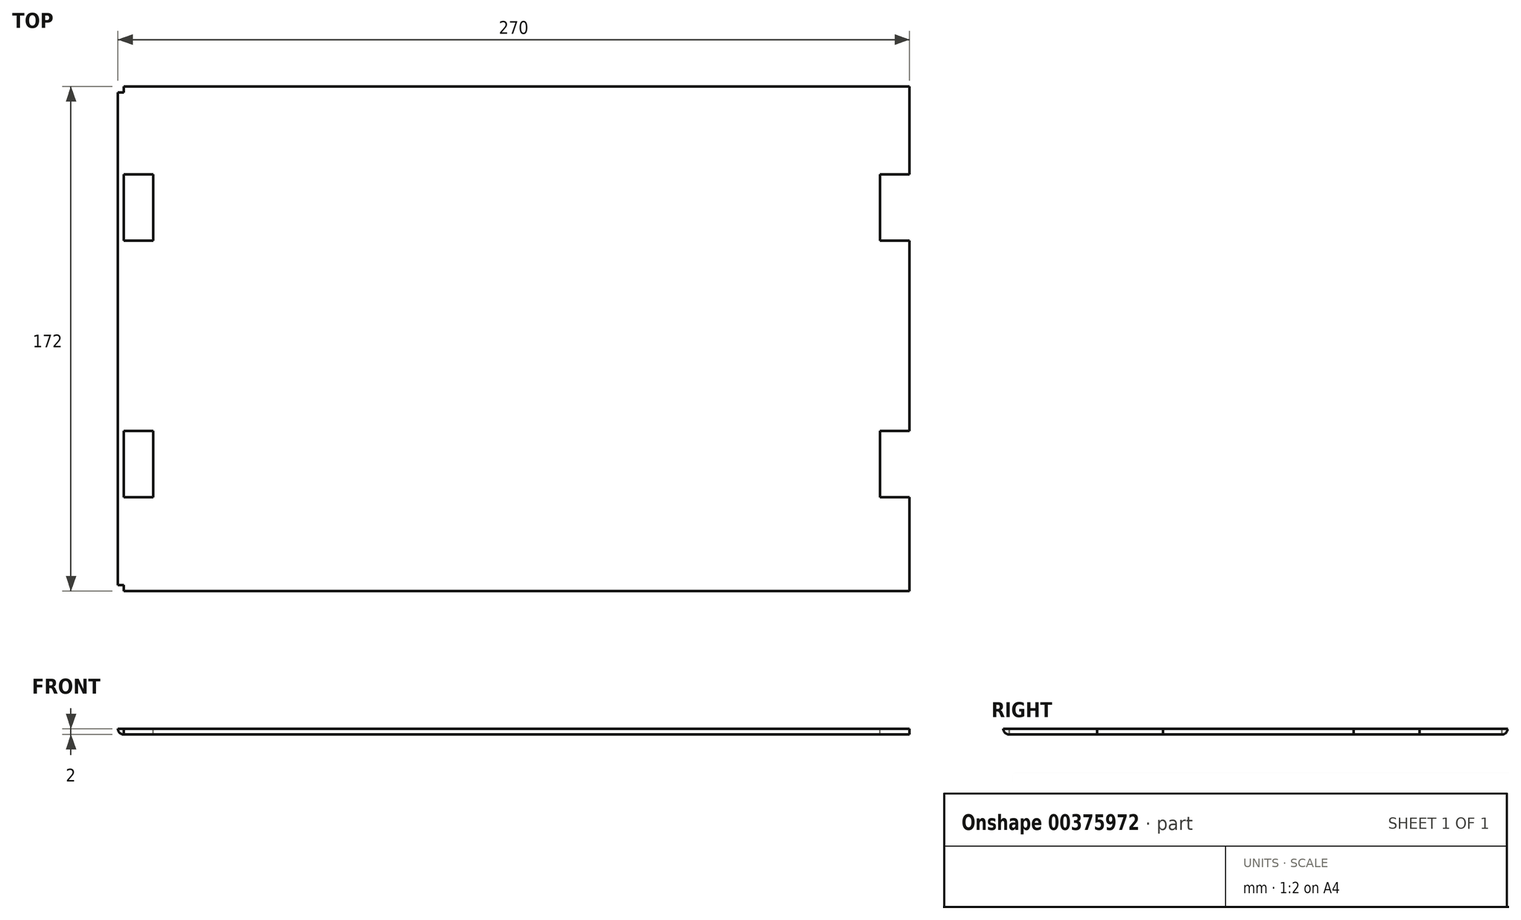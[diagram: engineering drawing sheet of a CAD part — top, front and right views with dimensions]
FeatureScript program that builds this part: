
annotation { "Feature Type Name" : "Feature", "Feature Type Description" : "" }
export const myFeature = defineFeature(function(context is Context, id is Id, definition is map)
    precondition{}
    {
        {
            var Q0;
            Q0=qCreatedBy(makeId("Top.planeOp"),FACE);
            var sketch = newSketch(context, id + "F0", { "sketchPlane" : qUnion([Q0])});
            skLineSegment(sketch, "E0.bottom", {"start": v(0, 0) * mm, "end": v(268, 0) * mm});
            skLineSegment(sketch, "E0.top", {"start": v(0, -168) * mm, "end": v(268, -168) * mm});
            skLineSegment(sketch, "E0.left", {"start": v(0, 0) * mm, "end": v(0, -168) * mm});
            skLineSegment(sketch, "E0.right", {"start": v(268, 0) * mm, "end": v(268, -168) * mm});
            skSolve(sketch);
        }
        {
            var Q0;
            Q0=makeQuery(id+"F0.imprint","IMPRINT",FACE,{"disambiguationData":[TD([[makeQuery(id+"F0.imprint","IMPRINT",EDGE,{"derivedFrom":sQuery(id+"F0.wireOp",EDGE,"E0.bottom")}),-1.0]])]});
            extrude(context, id + "F1", {"entities" : qUnion([Q0]), "depth" : 2 * mm});
        }
        {
            var Q0;
            Q0=makeQuery(id+"F1.opExtrude","SWEPT_FACE",FACE,{"disambiguationData":[OSD([sQuery(id+"F0.wireOp",EDGE,"E0.right")])]});
            var sketch = newSketch(context, id + "F2", { "sketchPlane" : qUnion([Q0])});
            skCircle(sketch, "E1", {"center": v(-168, 2) * mm, "radius": 2 * mm});
            skLineSegment(sketch, "E2", {"start": v(-168, 2) * mm, "end": v(-170, 2) * mm});
            skLineSegment(sketch, "E3", {"start": v(-168, 2) * mm, "end": v(-168, 0) * mm});
            skSolve(sketch);
        }
        {
            var Q0;
            {var subQ2=sQuery(id+"F2.wireOp",EDGE,"E2");Q0=makeQuery(id+"F2.imprint","IMPRINT",FACE,{"disambiguationData":[TD([[makeQuery(id+"F2.imprint","IMPRINT",EDGE,{"derivedFrom":subQ2}),1.0]])]});}
            extrude(context, id + "F3", {"entities" : qUnion([Q0]), "operationType" : NewBodyOperationType.ADD, "oppositeDirection" : true, "depth" : 268 * mm});
        }
        {
            var Q0;
            Q0=makeQuery(id+"F1.opExtrude","SWEPT_FACE",FACE,{"disambiguationData":[OSD([sQuery(id+"F0.wireOp",EDGE,"E0.bottom")])]});
            var sketch = newSketch(context, id + "F4", { "sketchPlane" : qUnion([Q0])});
            skCircle(sketch, "E4", {"center": v(-268, 2) * mm, "radius": 2 * mm});
            skLineSegment(sketch, "E5", {"start": v(-268, 2) * mm, "end": v(-270, 2) * mm});
            skLineSegment(sketch, "E6", {"start": v(-270, 2) * mm, "end": v(-268, 2) * mm});
            skLineSegment(sketch, "E7", {"start": v(-268, 0) * mm, "end": v(-268, 2) * mm});
            skCircle(sketch, "E8", {"center": v(0, 2) * mm, "radius": 2 * mm});
            skLineSegment(sketch, "E9", {"start": v(0, 2) * mm, "end": v(2, 2) * mm});
            skLineSegment(sketch, "E10", {"start": v(0, 2) * mm, "end": v(0, 0) * mm});
            skSolve(sketch);
        }
        {
            var Q0;
            Q0=makeQuery(id+"F3.boolean.opBoolean","MERGE",FACE,{"derivedFrom":[makeQuery(id+"F1.opExtrude","SWEPT_FACE",FACE,{"disambiguationData":[OSD([sQuery(id+"F0.wireOp",EDGE,"E0.right")])]}),makeQuery(id+"F3.opExtrude","CAP_FACE",FACE,{"disambiguationData":[OSD([sQuery(id+"F2.wireOp",EDGE,"E1"),sQuery(id+"F2.wireOp",EDGE,"E2"),sQuery(id+"F2.wireOp",EDGE,"E3")])],"isStart":true})]});
            var sketch = newSketch(context, id + "F5", { "sketchPlane" : qUnion([Q0])});
            skCircle(sketch, "E11", {"center": v(0, 2) * mm, "radius": 2 * mm});
            skLineSegment(sketch, "E12", {"start": v(0, 2) * mm, "end": v(2, 2) * mm});
            skLineSegment(sketch, "E13", {"start": v(0, 2) * mm, "end": v(0, 0) * mm});
            skSolve(sketch);
        }
        {
            var Q0;
            {var subQ2=sQuery(id+"F4.wireOp",EDGE,"E9");Q0=makeQuery(id+"F4.imprint","IMPRINT",FACE,{"disambiguationData":[TD([[makeQuery(id+"F4.imprint","IMPRINT",EDGE,{"derivedFrom":subQ2}),-1.0]])]});}
            var Q1;
            {var subQ2=sQuery(id+"F4.wireOp",EDGE,"E6");Q1=makeQuery(id+"F4.imprint","IMPRINT",FACE,{"disambiguationData":[TD([[makeQuery(id+"F4.imprint","IMPRINT",EDGE,{"derivedFrom":subQ2}),-1.0]])]});}
            extrude(context, id + "F6", {"entities" : qUnion([Q0, Q1]), "operationType" : NewBodyOperationType.ADD, "oppositeDirection" : true, "depth" : 168 * mm});
        }
        {
            var Q0;
            {var subQ2=sQuery(id+"F5.wireOp",EDGE,"E12");Q0=makeQuery(id+"F5.imprint","IMPRINT",FACE,{"disambiguationData":[TD([[makeQuery(id+"F5.imprint","IMPRINT",EDGE,{"derivedFrom":subQ2}),-1.0]])]});}
            extrude(context, id + "F7", {"entities" : qUnion([Q0]), "operationType" : NewBodyOperationType.ADD, "oppositeDirection" : true, "depth" : 268 * mm});
        }
        {
            var Q0;
            Q0=makeQuery(id+"F7.boolean.opBoolean","MERGE",FACE,{"derivedFrom":[makeQuery(id+"F6.boolean.opBoolean","MERGE",FACE,{"derivedFrom":[makeQuery(id+"F3.boolean.opBoolean","MERGE",FACE,{"derivedFrom":[makeQuery(id+"F1.opExtrude","CAP_FACE",FACE,{"disambiguationData":[OSD([sQuery(id+"F0.wireOp",EDGE,"E0.bottom"),sQuery(id+"F0.wireOp",EDGE,"E0.top"),sQuery(id+"F0.wireOp",EDGE,"E0.left"),sQuery(id+"F0.wireOp",EDGE,"E0.right")])],"isStart":false}),makeQuery(id+"F3.opExtrude","SWEPT_FACE",FACE,{"disambiguationData":[OSD([sQuery(id+"F2.wireOp",EDGE,"E2")])]})]}),makeQuery(id+"F6.opExtrude","SWEPT_FACE",FACE,{"disambiguationData":[OSD([sQuery(id+"F4.wireOp",EDGE,"E6")])]}),makeQuery(id+"F6.opExtrude","SWEPT_FACE",FACE,{"disambiguationData":[OSD([sQuery(id+"F4.wireOp",EDGE,"E9")])]})]}),makeQuery(id+"F7.opExtrude","SWEPT_FACE",FACE,{"disambiguationData":[OSD([sQuery(id+"F5.wireOp",EDGE,"E12")])]})]});
            var sketch = newSketch(context, id + "F8", { "sketchPlane" : qUnion([Q0])});
            skLineSegment(sketch, "E14.bottom", {"start": v(0, -28) * mm, "end": v(10, -28) * mm});
            skLineSegment(sketch, "E14.top", {"start": v(0, -50.5) * mm, "end": v(10, -50.5) * mm});
            skLineSegment(sketch, "E14.left", {"start": v(0, -28) * mm, "end": v(0, -50.5) * mm});
            skLineSegment(sketch, "E14.right", {"start": v(10, -28) * mm, "end": v(10, -50.5) * mm});
            skLineSegment(sketch, "E15.bottom", {"start": v(0, -138) * mm, "end": v(10, -138) * mm});
            skLineSegment(sketch, "E15.top", {"start": v(0, -115.5) * mm, "end": v(10, -115.5) * mm});
            skLineSegment(sketch, "E15.left", {"start": v(0, -138) * mm, "end": v(0, -115.5) * mm});
            skLineSegment(sketch, "E15.right", {"start": v(10, -138) * mm, "end": v(10, -115.5) * mm});
            skLineSegment(sketch, "E16", {"start": v(134, 2) * mm, "end": v(134, -170) * mm});
            skLineSegment(sketch, "E17.MirrorCS", {"start": v(258, -28) * mm, "end": v(258, -50.5) * mm});
            skLineSegment(sketch, "E18.MirrorCS", {"start": v(268, -28) * mm, "end": v(258, -28) * mm});
            skLineSegment(sketch, "E19.MirrorCS", {"start": v(268, -28) * mm, "end": v(268, -50.5) * mm});
            skLineSegment(sketch, "E20.MirrorCS", {"start": v(268, -50.5) * mm, "end": v(258, -50.5) * mm});
            skLineSegment(sketch, "E21.MirrorCS", {"start": v(268, -115.5) * mm, "end": v(258, -115.5) * mm});
            skLineSegment(sketch, "E22.MirrorCS", {"start": v(268, -138) * mm, "end": v(268, -115.5) * mm});
            skLineSegment(sketch, "E23.MirrorCS", {"start": v(258, -138) * mm, "end": v(258, -115.5) * mm});
            skLineSegment(sketch, "E24.MirrorCS", {"start": v(268, -138) * mm, "end": v(258, -138) * mm});
            skSolve(sketch);
        }
        {
            var Q0;
            Q0=makeQuery(id+"F8.imprint","IMPRINT",FACE,{"disambiguationData":[TD([[makeQuery(id+"F8.imprint","IMPRINT",EDGE,{"derivedFrom":sQuery(id+"F8.wireOp",EDGE,"E17.MirrorCS")}),1.0]])]});
            var Q1;
            Q1=makeQuery(id+"F8.imprint","IMPRINT",FACE,{"disambiguationData":[TD([[makeQuery(id+"F8.imprint","IMPRINT",EDGE,{"derivedFrom":sQuery(id+"F8.wireOp",EDGE,"E21.MirrorCS")}),1.0]])]});
            var Q2;
            Q2=makeQuery(id+"F8.imprint","IMPRINT",FACE,{"disambiguationData":[TD([[makeQuery(id+"F8.imprint","IMPRINT",EDGE,{"derivedFrom":sQuery(id+"F8.wireOp",EDGE,"E15.bottom")}),1.0]])]});
            var Q3;
            Q3=makeQuery(id+"F8.imprint","IMPRINT",FACE,{"disambiguationData":[TD([[makeQuery(id+"F8.imprint","IMPRINT",EDGE,{"derivedFrom":sQuery(id+"F8.wireOp",EDGE,"E14.bottom")}),-1.0]])]});
            extrude(context, id + "F9", {"entities" : qUnion([Q0, Q1, Q2, Q3]), "operationType" : NewBodyOperationType.REMOVE, "oppositeDirection" : true, "depth" : 25 * mm});
        }
    });
